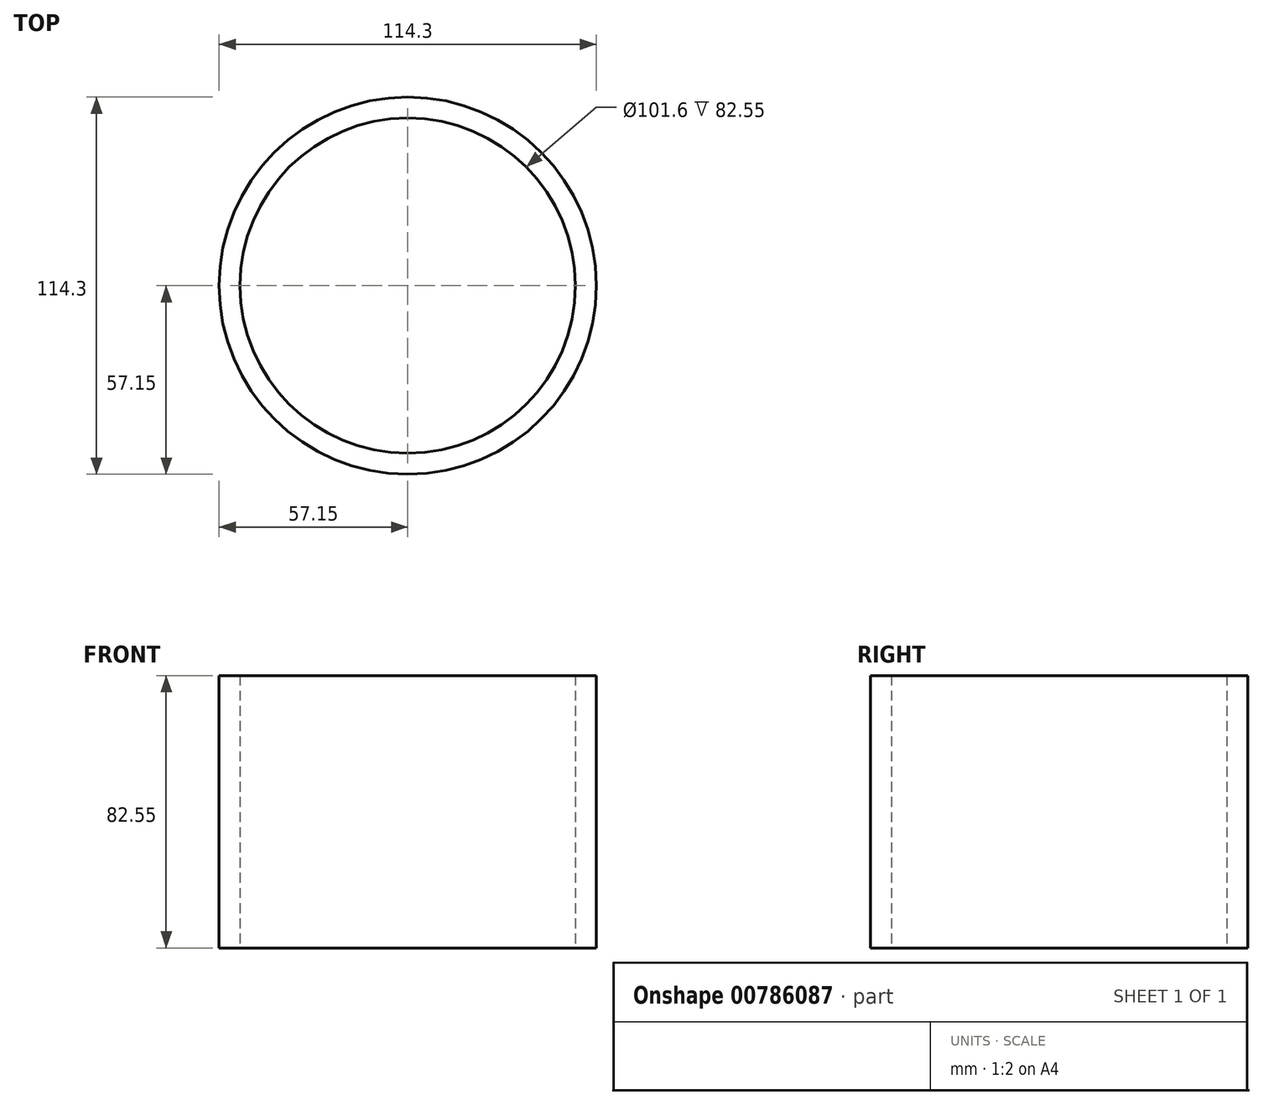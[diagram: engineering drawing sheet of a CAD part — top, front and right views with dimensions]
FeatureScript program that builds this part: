
annotation { "Feature Type Name" : "Feature", "Feature Type Description" : "" }
export const myFeature = defineFeature(function(context is Context, id is Id, definition is map)
    precondition{}
    {
        {
            var Q0;
            Q0=qCreatedBy(makeId("Top.planeOp"),FACE);
            var sketch = newSketch(context, id + "F0", { "sketchPlane" : qUnion([Q0])});
            skCircle(sketch, "E0", {"center": v(0, 0) * mm, "radius": 50.8 * mm});
            skCircle(sketch, "E1", {"center": v(0, 0) * mm, "radius": 57.15 * mm});
            skSolve(sketch);
        }
        {
            var Q0;
            Q0 = qSketchRegion(id + "F0", true);
            extrude(context, id + "F1", {"entities" : qUnion([Q0]), "depth" : 82.55 * mm, "offsetDistance" : 25.4 * mm});
        }
    });
